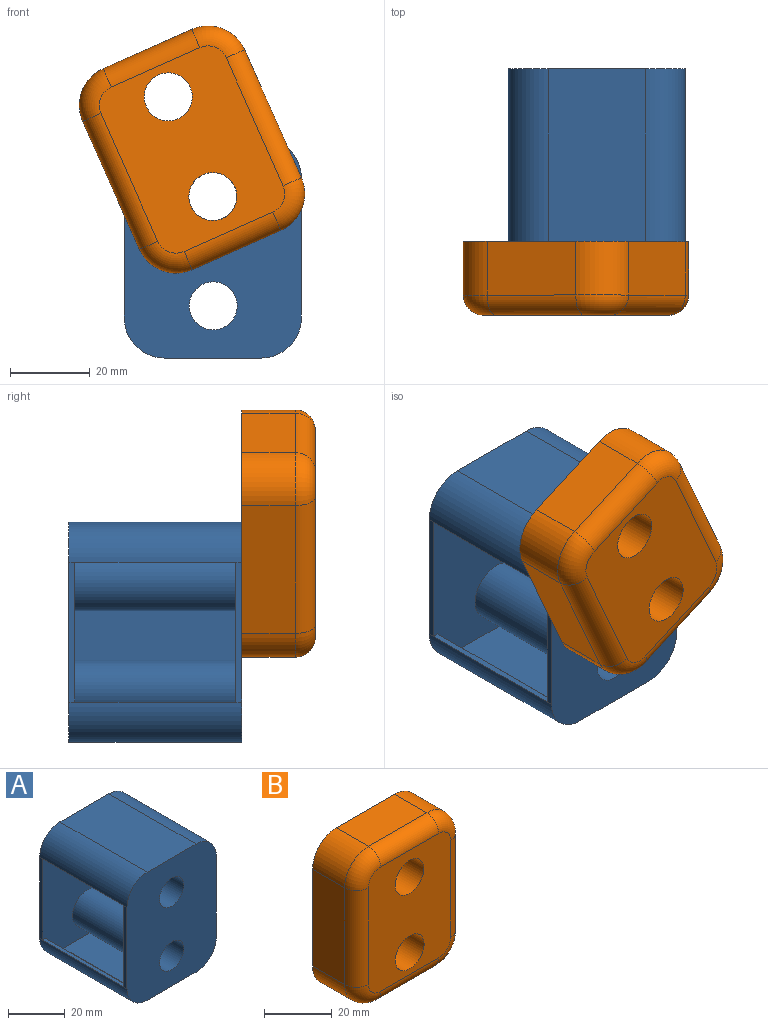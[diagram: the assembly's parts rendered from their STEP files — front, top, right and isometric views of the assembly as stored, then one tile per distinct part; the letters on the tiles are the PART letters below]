
ASSEMBLY  parts=2 mates=1
PART A: 26 faces, bbox 44.3x43.3x55 mm
  f0: plane 35x1.5mm, normal (-1,0,0), area 52.5mm2, adj f8,f10,f11,f21
  f1: plane 43.26x35mm, normal (1,0,0), area 1514.2mm2, adj f7,f8,f9,f12
  f2: plane 43.26x24.27mm, normal (0,0,1), area 1049.9mm2, adj f7,f8,f9,f10
  f3: plane 35x1.5mm, normal (-1,0,0), area 52.5mm2, adj f7,f10,f11,f20
  f4: plane 43.26x24.27mm, normal (0,0,-1), area 1049.9mm2, adj f7,f8,f11,f12
  f5: cylinder r=6mm len=43.26mm, axis (0,1,0), area 1631mm2, adj f7,f8
  f6: cylinder r=6mm len=43.26mm, axis (0,1,0), area 1631mm2, adj f7,f8
  f7: plane 55x44.27mm, normal (0,-1,0), area 2122.7mm2, adj f1,f2,f3,f4,f5,f6,f9,f10
  f8: plane 55x44.27mm, normal (0,1,0), area 2122.7mm2, adj f0,f1,f2,f4,f5,f6,f9,f10
  f9: cylinder r=10mm len=43.26mm, axis (0,-1,0), area 679.6mm2, adj f1,f2,f7,f8
  f10: cylinder r=10mm len=43.26mm, axis (0,1,0), area 679.6mm2, adj f0,f2,f3,f7,f8,f14
  f11: cylinder r=10mm len=43.26mm, axis (0,-1,0), area 679.6mm2, adj f0,f3,f4,f7,f8,f13
  f12: cylinder r=10mm len=43.26mm, axis (0,1,0), area 679.6mm2, adj f1,f4,f7,f8
  f13: plane 40.26x1.5mm, normal (0,0,1), area 60.4mm2, adj f11,f20,f21,f24
  f14: plane 40.26x1.5mm, normal (0,0,-1), area 60.4mm2, adj f10,f20,f21,f23
  f15: plane 40.26x35mm, normal (-1,0,0), area 1409.2mm2, adj f20,f21,f22,f25
  f16: plane 40.26x24.27mm, normal (0,0,-1), area 977.1mm2, adj f20,f21,f22,f23
  f17: plane 40.26x24.27mm, normal (0,0,1), area 977.1mm2, adj f20,f21,f24,f25
  f18: cylinder r=7.5mm len=40.26mm, axis (0,1,0), area 1897.4mm2, adj f20,f21
  f19: cylinder r=7.5mm len=40.26mm, axis (0,1,0), area 1897.4mm2, adj f20,f21
  f20: plane 52x42.77mm, normal (0,1,0), area 1783mm2, adj f3,f13,f14,f15,f16,f17,f18,f19
  f21: plane 52x42.77mm, normal (0,-1,0), area 1783mm2, adj f0,f13,f14,f15,f16,f17,f18,f19
  f22: cylinder r=8.5mm len=40.26mm, axis (0,-1,0), area 537.6mm2, adj f15,f16,f20,f21
  f23: cylinder r=8.5mm len=40.26mm, axis (0,1,0), area 537.6mm2, adj f14,f16,f20,f21
  f24: cylinder r=8.5mm len=40.26mm, axis (0,-1,0), area 537.6mm2, adj f13,f17,f20,f21
  f25: cylinder r=8.5mm len=40.26mm, axis (0,1,0), area 537.6mm2, adj f15,f17,f20,f21
PART B: 41 faces, bbox 45.9x18.4x56.6 mm
  f0: plane 15x15mm, normal (0,1,0), area 63.6mm2, adj f11,f30
  f1: plane 55x44.27mm, normal (0,1,0), area 265mm2, adj f3,f4,f5,f6,f7,f8,f9,f10
  f2: plane 15x15mm, normal (0,1,0), area 63.6mm2, adj f12,f31
  f3: plane 35x13.4mm, normal (1,0,0), area 468.8mm2, adj f1,f4,f10,f16
  f4: cylinder r=10mm len=13.4mm, axis (0,1,0), area 210.4mm2, adj f1,f3,f5,f14
  f5: plane 24.27x13.4mm, normal (0,0,1), area 325.1mm2, adj f1,f4,f6,f15
  f6: cylinder r=10mm len=13.4mm, axis (0,1,0), area 210.4mm2, adj f1,f5,f7,f17
  f7: plane 35x13.4mm, normal (-1,0,0), area 468.8mm2, adj f1,f6,f8,f19
  f8: cylinder r=10mm len=13.4mm, axis (0,1,0), area 210.4mm2, adj f1,f7,f9,f21
  f9: plane 24.27x13.4mm, normal (0,0,-1), area 325.1mm2, adj f1,f8,f10,f20
  f10: cylinder r=10mm len=13.4mm, axis (0,1,0), area 210.4mm2, adj f1,f3,f9,f18
  f11: cylinder r=6mm len=18.4mm, axis (0,1,0), area 693.5mm2, adj f0,f13
  f12: cylinder r=6mm len=18.4mm, axis (0,1,0), area 693.5mm2, adj f2,f13
  f13: plane 45x34.27mm, normal (0,-1,0), area 1294.4mm2, adj f11,f12,f14,f15,f16,f17,f18,f19
  f14: torus R=5mm, axis (0,-1,0), area 101mm2, adj f4,f13,f15,f16
  f15: cylinder r=5mm len=24.27mm, axis (1,0,0), area 190.6mm2, adj f5,f13,f14,f17
  f16: cylinder r=5mm len=35mm, axis (0,0,-1), area 274.9mm2, adj f3,f13,f14,f18
  f17: torus R=5mm, axis (0,-1,0), area 101mm2, adj f6,f13,f15,f19
  f18: torus R=5mm, axis (0,-1,0), area 101mm2, adj f10,f13,f16,f20
  f19: cylinder r=5mm len=35mm, axis (0,0,1), area 274.9mm2, adj f7,f13,f17,f21
  f20: cylinder r=5mm len=24.27mm, axis (-1,0,0), area 190.6mm2, adj f9,f13,f18,f21
  f21: torus R=5mm, axis (0,-1,0), area 101mm2, adj f8,f13,f19,f20
  f22: plane 35x13.4mm, normal (-1,0,0), area 468.8mm2, adj f1,f23,f29,f35
  f23: cylinder r=8.5mm len=13.4mm, axis (0,1,0), area 178.9mm2, adj f1,f22,f24,f33
  f24: plane 24.27x13.4mm, normal (0,0,-1), area 325.1mm2, adj f1,f23,f25,f34
  f25: cylinder r=8.5mm len=13.4mm, axis (0,1,0), area 178.9mm2, adj f1,f24,f26,f36
  f26: plane 35x13.4mm, normal (1,0,0), area 468.8mm2, adj f1,f25,f27,f38
  f27: cylinder r=8.5mm len=13.4mm, axis (0,1,0), area 178.9mm2, adj f1,f26,f28,f40
  f28: plane 24.27x13.4mm, normal (0,0,1), area 325.1mm2, adj f1,f27,f29,f39
  f29: cylinder r=8.5mm len=13.4mm, axis (0,1,0), area 178.9mm2, adj f1,f22,f28,f37
  f30: cylinder r=7.5mm len=16.9mm, axis (0,1,0), area 796.2mm2, adj f0,f32
  f31: cylinder r=7.5mm len=16.9mm, axis (0,1,0), area 796.2mm2, adj f2,f32
  f32: plane 45x34.27mm, normal (0,1,0), area 1167.2mm2, adj f30,f31,f33,f34,f35,f36,f37,f38
  f33: torus R=5mm, axis (0,-1,0), area 62.4mm2, adj f23,f32,f34,f35
  f34: cylinder r=3.5mm len=24.27mm, axis (1,0,0), area 133.4mm2, adj f24,f32,f33,f36
  f35: cylinder r=3.5mm len=35mm, axis (0,0,-1), area 192.4mm2, adj f22,f32,f33,f37
  f36: torus R=5mm, axis (0,-1,0), area 62.4mm2, adj f25,f32,f34,f38
  f37: torus R=5mm, axis (0,-1,0), area 62.4mm2, adj f29,f32,f35,f39
  f38: cylinder r=3.5mm len=35mm, axis (0,0,1), area 192.4mm2, adj f26,f32,f36,f40
  f39: cylinder r=3.5mm len=24.27mm, axis (-1,0,0), area 133.4mm2, adj f28,f32,f37,f40
  f40: torus R=5mm, axis (0,-1,0), area 62.4mm2, adj f27,f32,f38,f39
PLACE A t=(-25.81,-146.53,-18.51)mm fixed
PLACE B rot(axis=(0,1,0),156.1deg) t=(0.2,-146.53,67.73)mm
MATE revolute A.f5 <-> B.f11  axis (0,-1,0) through (-3.68,-189.79,21.86)mm
